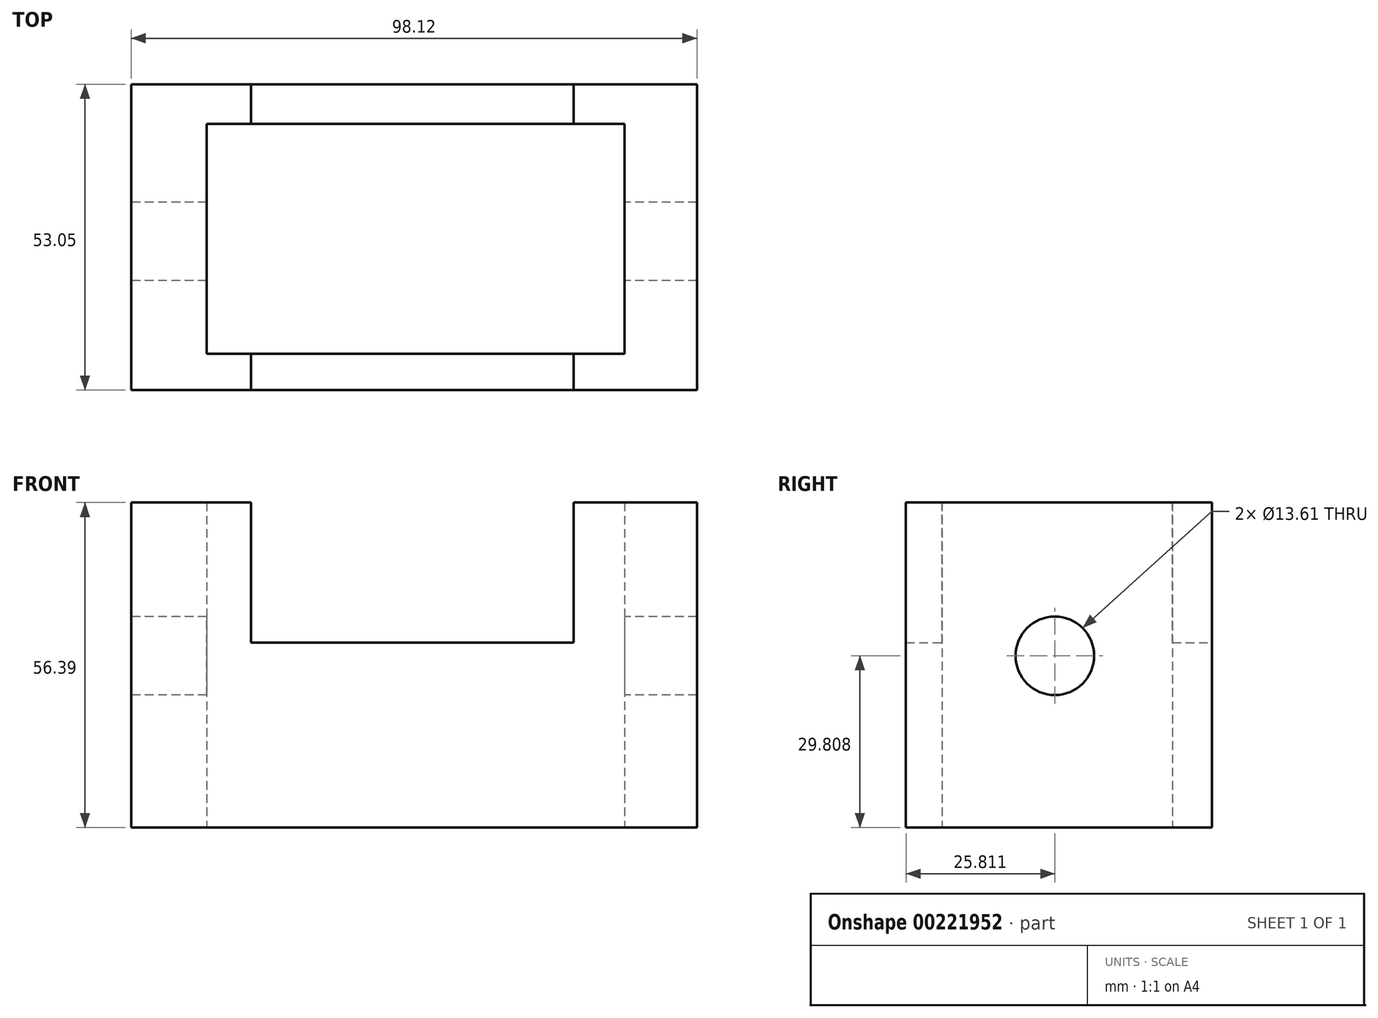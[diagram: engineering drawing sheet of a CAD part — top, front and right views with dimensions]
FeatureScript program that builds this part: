
annotation { "Feature Type Name" : "Feature", "Feature Type Description" : "" }
export const myFeature = defineFeature(function(context is Context, id is Id, definition is map)
    precondition{}
    {
        {
            var Q0;
            Q0=qCreatedBy(makeId("Top.planeOp"),FACE);
            var sketch = newSketch(context, id + "F0", { "sketchPlane" : qUnion([Q0])});
            skLineSegment(sketch, "E0.bottom", {"start": v(106.4, -66.03) * mm, "end": v(8.27, -66.03) * mm});
            skLineSegment(sketch, "E0.top", {"start": v(106.4, -12.98) * mm, "end": v(8.27, -12.98) * mm});
            skLineSegment(sketch, "E0.left", {"start": v(106.4, -66.03) * mm, "end": v(106.4, -12.98) * mm});
            skLineSegment(sketch, "E0.right", {"start": v(8.27, -66.03) * mm, "end": v(8.27, -12.98) * mm});
            skPoint(sketch, "E0.middle", {"position": v(57.33, -39.5) * mm});
            skSolve(sketch);
        }
        {
            var Q0;
            Q0 = qSketchRegion(id + "F0", true);
            extrude(context, id + "F1", {"entities" : qUnion([Q0]), "depth" : 56.4 * mm});
        }
        {
            var Q0;
            Q0=qCreatedBy(makeId("Top.planeOp"),FACE);
            var sketch = newSketch(context, id + "F2", { "sketchPlane" : qUnion([Q0])});
            skLineSegment(sketch, "E1.bottom", {"start": v(93.82, -59.76) * mm, "end": v(21.37, -59.76) * mm});
            skLineSegment(sketch, "E1.top", {"start": v(93.82, -19.82) * mm, "end": v(21.37, -19.82) * mm});
            skLineSegment(sketch, "E1.left", {"start": v(93.82, -59.76) * mm, "end": v(93.82, -19.82) * mm});
            skLineSegment(sketch, "E1.right", {"start": v(21.37, -59.76) * mm, "end": v(21.37, -19.82) * mm});
            skPoint(sketch, "E1.middle", {"position": v(57.6, -39.8) * mm});
            skSolve(sketch);
        }
        {
            var Q0;
            Q0 = qSketchRegion(id + "F2", true);
            extrude(context, id + "F3", {"entities" : qUnion([Q0]), "operationType" : NewBodyOperationType.REMOVE, "endBound" : BoundingType.THROUGH_ALL, "depth" : 84.84 * mm});
        }
        {
            var Q0;
            Q0=qCreatedBy(makeId("Right.planeOp"),FACE);
            var sketch = newSketch(context, id + "F4", { "sketchPlane" : qUnion([Q0])});
            skCircle(sketch, "E2", {"center": v(-40.22, 29.8) * mm, "radius": 6.8 * mm});
            skSolve(sketch);
        }
        {
            var Q0;
            Q0 = qSketchRegion(id + "F4", true);
            extrude(context, id + "F5", {"entities" : qUnion([Q0]), "operationType" : NewBodyOperationType.REMOVE, "endBound" : BoundingType.THROUGH_ALL, "depth" : 140.72 * mm});
        }
        {
            var Q0;
            Q0=qCreatedBy(makeId("Front.planeOp"),FACE);
            var sketch = newSketch(context, id + "F6", { "sketchPlane" : qUnion([Q0])});
            skLineSegment(sketch, "E3", {"start": v(40.2, 62.61) * mm, "end": v(29.07, 62.61) * mm});
            skLineSegment(sketch, "E4", {"start": v(29.07, 62.61) * mm, "end": v(29.07, 32.09) * mm});
            skLineSegment(sketch, "E5", {"start": v(29.07, 32.09) * mm, "end": v(84.98, 32.09) * mm});
            skLineSegment(sketch, "E6", {"start": v(84.98, 32.09) * mm, "end": v(84.98, 64.9) * mm});
            skLineSegment(sketch, "E7", {"start": v(84.98, 64.9) * mm, "end": v(40.2, 62.61) * mm});
            skSolve(sketch);
        }
        {
            var Q0;
            Q0 = qSketchRegion(id + "F6", true);
            extrude(context, id + "F7", {"entities" : qUnion([Q0]), "operationType" : NewBodyOperationType.REMOVE, "depth" : 101.6 * mm});
        }
    });
